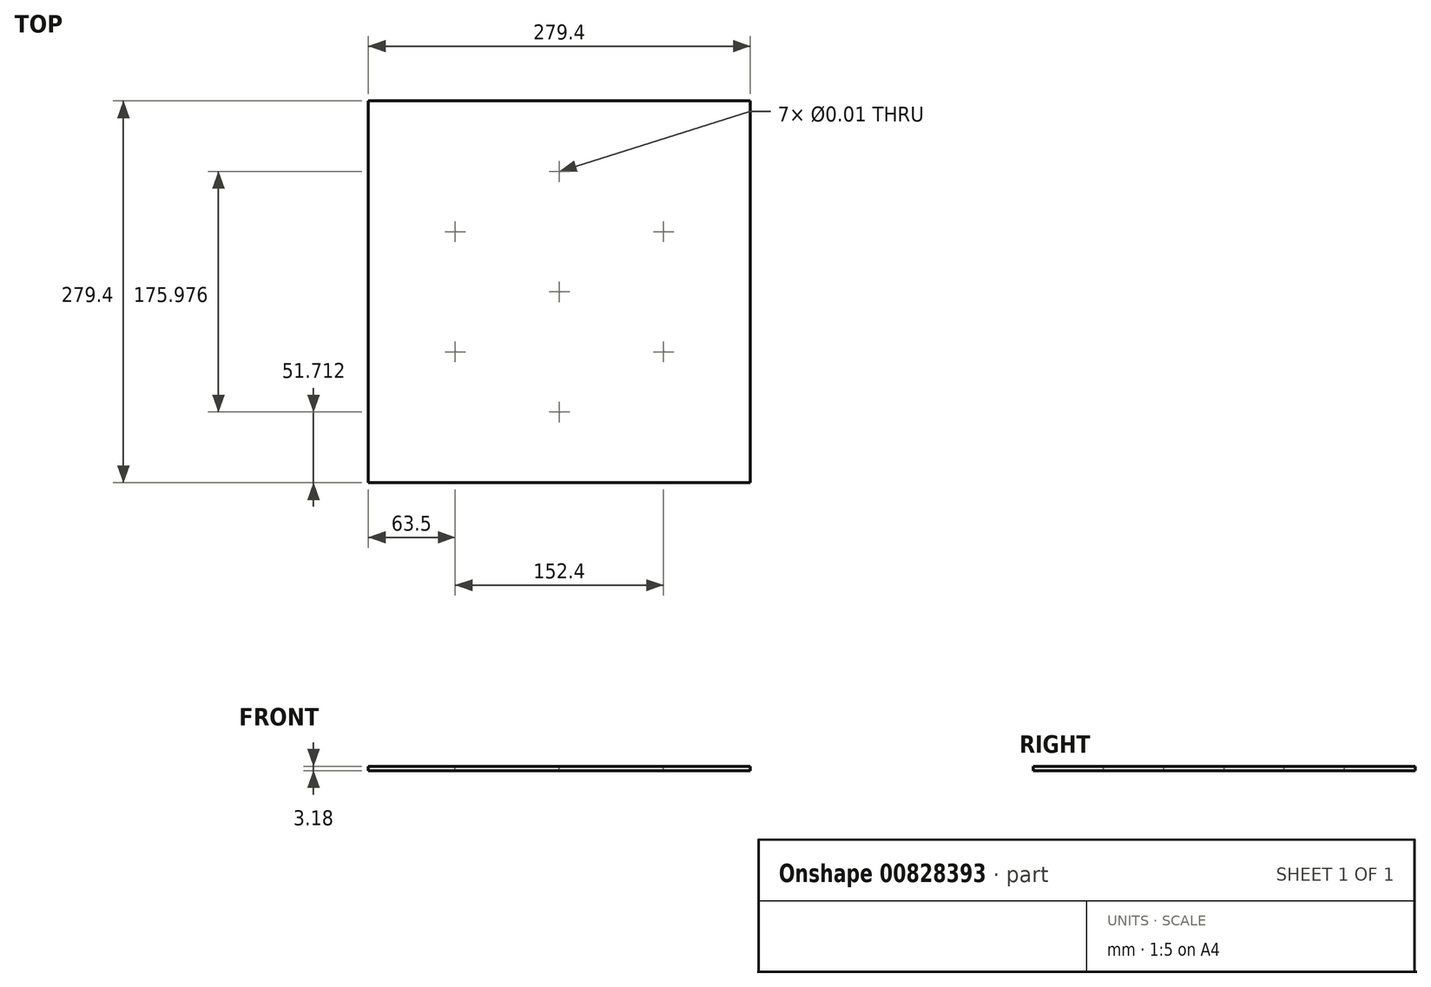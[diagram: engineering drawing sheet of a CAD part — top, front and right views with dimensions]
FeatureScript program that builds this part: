
annotation { "Feature Type Name" : "Feature", "Feature Type Description" : "" }
export const myFeature = defineFeature(function(context is Context, id is Id, definition is map)
    precondition{}
    {
        {
            var Q0;
            Q0=qCreatedBy(makeId("Top.planeOp"),FACE);
            var sketch = newSketch(context, id + "F0", { "sketchPlane" : qUnion([Q0])});
            skLineSegment(sketch, "E0.bottom", {"start": v(-139.7, -139.7) * mm, "end": v(139.7, -139.7) * mm});
            skLineSegment(sketch, "E0.top", {"start": v(-139.7, 139.7) * mm, "end": v(139.7, 139.7) * mm});
            skLineSegment(sketch, "E0.left", {"start": v(-139.7, -139.7) * mm, "end": v(-139.7, 139.7) * mm});
            skLineSegment(sketch, "E0.right", {"start": v(139.7, -139.7) * mm, "end": v(139.7, 139.7) * mm});
            skPoint(sketch, "E0.middle", {"position": v(0, 0) * mm});
            skSolve(sketch);
        }
        {
            var Q0;
            Q0 = qSketchRegion(id + "F0", true);
            extrude(context, id + "F1", {"entities" : qUnion([Q0]), "depth" : 3.17 * mm, "offsetDistance" : 25.4 * mm});
        }
        {
            var Q0;
            Q0=makeQuery(id+"F1.opExtrude","CAP_FACE",FACE,{"disambiguationData":[OSD([sQuery(id+"F0.wireOp",EDGE,"E0.bottom"),sQuery(id+"F0.wireOp",EDGE,"E0.top"),sQuery(id+"F0.wireOp",EDGE,"E0.left"),sQuery(id+"F0.wireOp",EDGE,"E0.right")])],"isStart":false});
            var sketch = newSketch(context, id + "F2", { "sketchPlane" : qUnion([Q0])});
            skCircle(sketch, "E1.cCircle", {"center": v(0, 0) * mm, "radius": 76.2 * mm, "construction": true});
            skLineSegment(sketch, "E1.0", {"start": v(0, 87.99) * mm, "end": v(76.2, 44) * mm});
            skLineSegment(sketch, "E1.1", {"start": v(76.2, 44) * mm, "end": v(76.2, -44) * mm});
            skLineSegment(sketch, "E1.2", {"start": v(76.2, -44) * mm, "end": v(0, -87.99) * mm});
            skLineSegment(sketch, "E1.3", {"start": v(0, -87.99) * mm, "end": v(-76.2, -44) * mm});
            skLineSegment(sketch, "E1.4", {"start": v(-76.2, -44) * mm, "end": v(-76.2, 44) * mm});
            skLineSegment(sketch, "E1.5", {"start": v(-76.2, 44) * mm, "end": v(0, 87.99) * mm});
            skPoint(sketch, "E1.0.midPoint", {"position": v(38.1, 66) * mm});
            skSolve(sketch);
        }
        {
            var Q0;
            Q0=sQuery(id+"F2.wireOp",VERTEX,"E1.0.start");
            var Q1;
            Q1=sQuery(id+"F2.wireOp",VERTEX,"E1.0.end");
            var Q2;
            Q2=sQuery(id+"F2.wireOp",VERTEX,"E1.1.end");
            var Q3;
            Q3=sQuery(id+"F2.wireOp",VERTEX,"E1.2.end");
            var Q4;
            Q4=sQuery(id+"F2.wireOp",VERTEX,"E1.3.end");
            var Q5;
            Q5=sQuery(id+"F2.wireOp",VERTEX,"E1.4.end");
            var Q6;
            Q6=sQuery(id+"F2.wireOp",VERTEX,"E1.cCircle.center");
            var Q7;
            Q7=makeQuery(id+"F1.opExtrude","SWEPT_BODY",BODY,{"disambiguationData":[OSD([sQuery(id+"F0.wireOp",EDGE,"E0.bottom"),sQuery(id+"F0.wireOp",EDGE,"E0.top"),sQuery(id+"F0.wireOp",EDGE,"E0.left"),sQuery(id+"F0.wireOp",EDGE,"E0.right")])]});
            hole(context, id + "F3", {"style" : HoleStyle.SIMPLE, "endStyle" : HoleEndStyle.THROUGH, "standardTappedOrClearance" : lookupTablePath({ "standard" : "ANSI", "size" : "3/8 (0.38)", "type" : "Drilled" }), "standardBlindInLast" : lookupTablePath({ "standard" : "ANSI", "size" : "3/8", "type" : "Drilled" }), "holeDiameter" : 3 / 203.2 * mm, "majorDiameter" : 9.52 * mm, "isTappedThrough" : true, "tappedDepth" : 12.7 * mm, "tapClearance" : 3, "locations" : qUnion([Q0, Q1, Q2, Q3, Q4, Q5, Q6]), "scope" : qUnion([Q7])});
        }
    });
